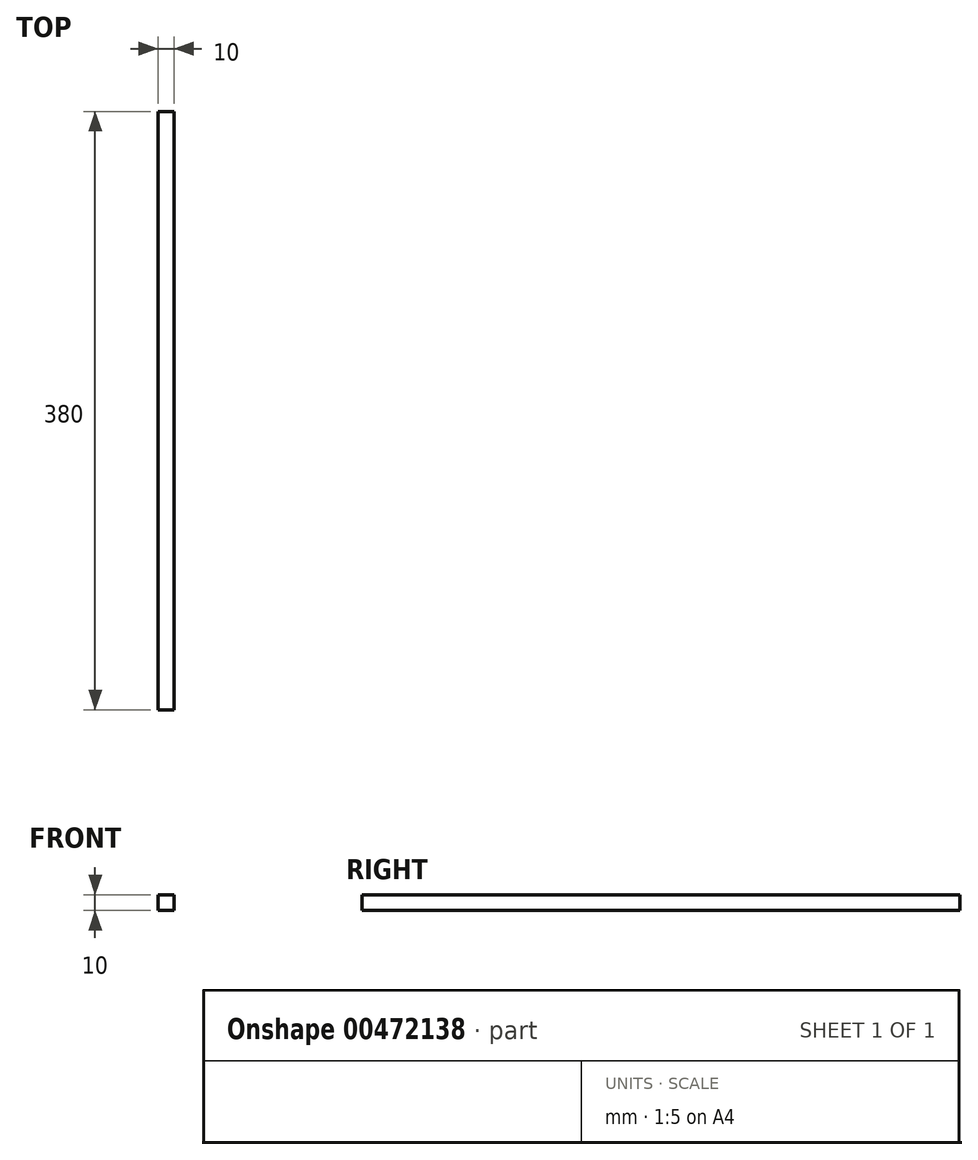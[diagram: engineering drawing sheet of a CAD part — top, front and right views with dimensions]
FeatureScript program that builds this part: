
annotation { "Feature Type Name" : "Feature", "Feature Type Description" : "" }
export const myFeature = defineFeature(function(context is Context, id is Id, definition is map)
    precondition{}
    {
        {
            var Q0;
            Q0=qCreatedBy(makeId("Front.planeOp"),FACE);
            var sketch = newSketch(context, id + "F0", { "sketchPlane" : qUnion([Q0])});
            skLineSegment(sketch, "E0.bottom", {"start": v(5, -5) * mm, "end": v(-5, -5) * mm});
            skLineSegment(sketch, "E0.top", {"start": v(5, 5) * mm, "end": v(-5, 5) * mm});
            skLineSegment(sketch, "E0.left", {"start": v(5, -5) * mm, "end": v(5, 5) * mm});
            skLineSegment(sketch, "E0.right", {"start": v(-5, -5) * mm, "end": v(-5, 5) * mm});
            skPoint(sketch, "E0.middle", {"position": v(0, 0) * mm});
            skSolve(sketch);
        }
        {
            var Q0;
            Q0=makeQuery(id+"F0.imprint","IMPRINT",FACE,{"disambiguationData":[TD([[makeQuery(id+"F0.imprint","IMPRINT",EDGE,{"derivedFrom":sQuery(id+"F0.wireOp",EDGE,"E0.bottom")}),-1.0]])]});
            extrude(context, id + "F1", {"entities" : qUnion([Q0]), "depth" : 380 * mm});
        }
    });
